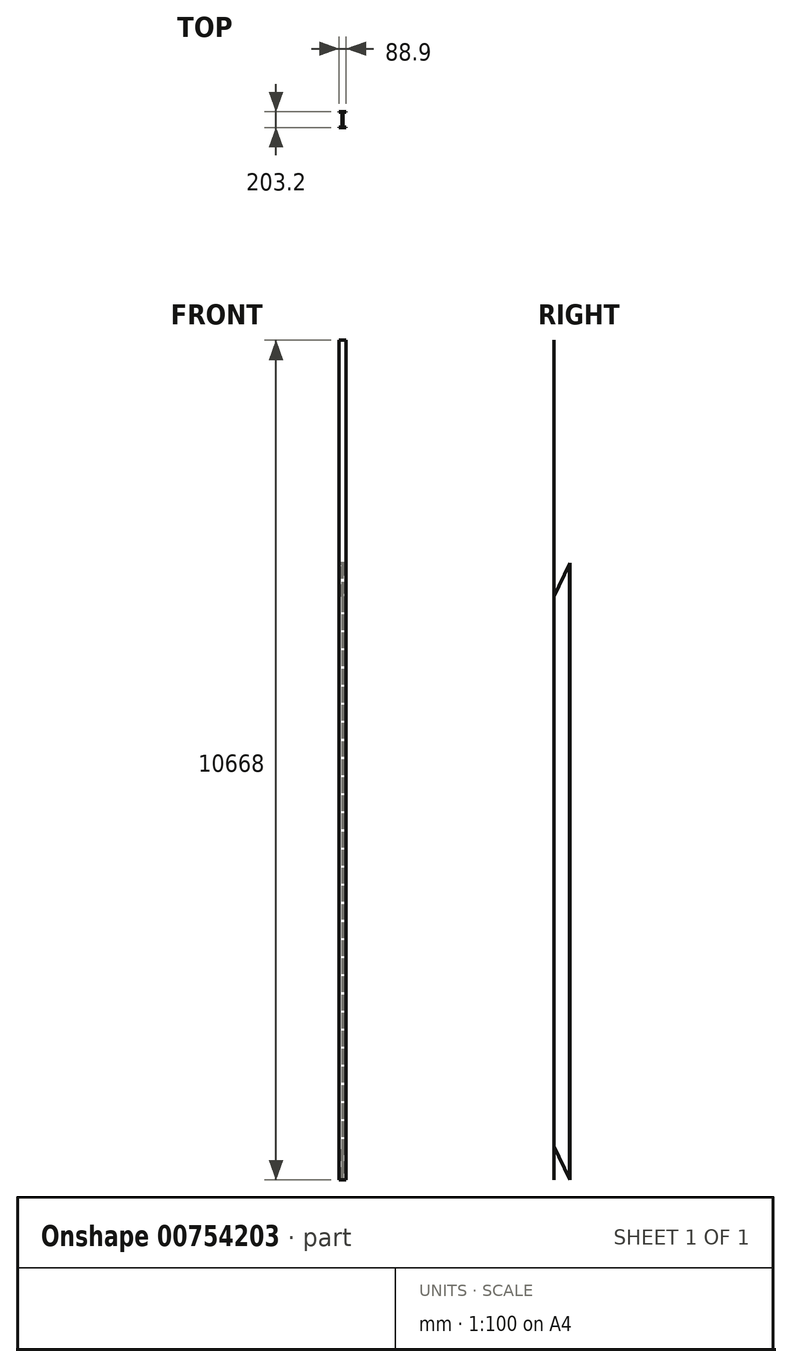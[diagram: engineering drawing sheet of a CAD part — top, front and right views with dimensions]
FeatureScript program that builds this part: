
annotation { "Feature Type Name" : "Feature", "Feature Type Description" : "" }
export const myFeature = defineFeature(function(context is Context, id is Id, definition is map)
    precondition{}
    {
        {
            var Q0;
            Q0=qCreatedBy(makeId("Top.planeOp"),FACE);
            var sketch = newSketch(context, id + "F0", { "sketchPlane" : qUnion([Q0])});
            skLineSegment(sketch, "E0.bottom", {"start": v(44.45, 101.6) * mm, "end": v(-44.45, 101.6) * mm});
            skLineSegment(sketch, "E0.top", {"start": v(44.45, -101.6) * mm, "end": v(-44.45, -101.6) * mm});
            skLineSegment(sketch, "E0.left", {"start": v(44.45, 101.6) * mm, "end": v(44.45, -101.6) * mm});
            skLineSegment(sketch, "E0.right", {"start": v(-44.45, 101.6) * mm, "end": v(-44.45, -101.6) * mm});
            skPoint(sketch, "E0.middle", {"position": v(0, 0) * mm});
            skSolve(sketch);
        }
        {
            var Q0;
            Q0=makeQuery(id+"F0.imprint","IMPRINT",FACE,{"disambiguationData":[TD([[makeQuery(id+"F0.imprint","IMPRINT",EDGE,{"derivedFrom":sQuery(id+"F0.wireOp",EDGE,"E0.bottom")}),1.0]])]});
            extrude(context, id + "F1", {"entities" : qUnion([Q0]), "depth" : 10668 * mm, "offsetDistance" : 25.4 * mm});
        }
        {
            var Q0;
            Q0=qCreatedBy(makeId("Top.planeOp"),FACE);
            var sketch = newSketch(context, id + "F2", { "sketchPlane" : qUnion([Q0])});
            skLineSegment(sketch, "E1.0.0", {"start": v(44.45, -101.6) * mm, "end": v(-44.45, -101.6) * mm, "construction": true});
            skLineSegment(sketch, "E1.0.1", {"start": v(-44.45, -101.6) * mm, "end": v(-44.45, 101.6) * mm, "construction": true});
            skLineSegment(sketch, "E1.0.2", {"start": v(-44.45, 101.6) * mm, "end": v(44.45, 101.6) * mm, "construction": true});
            skLineSegment(sketch, "E1.0.3", {"start": v(44.45, 101.6) * mm, "end": v(44.45, -101.6) * mm, "construction": true});
            skLineSegment(sketch, "E2.bottom", {"start": v(-44.45, -96.52) * mm, "end": v(-4.76, -96.52) * mm});
            skLineSegment(sketch, "E2.top", {"start": v(-44.45, 96.52) * mm, "end": v(-4.76, 96.52) * mm});
            skLineSegment(sketch, "E2.left", {"start": v(-44.45, -96.52) * mm, "end": v(-44.45, 96.52) * mm});
            skLineSegment(sketch, "E2.right", {"start": v(-4.76, -96.52) * mm, "end": v(-4.76, 96.52) * mm});
            skLineSegment(sketch, "E3.bottom", {"start": v(44.45, -96.52) * mm, "end": v(4.76, -96.52) * mm});
            skLineSegment(sketch, "E3.top", {"start": v(44.45, 96.52) * mm, "end": v(4.76, 96.52) * mm});
            skLineSegment(sketch, "E3.left", {"start": v(44.45, -96.52) * mm, "end": v(44.45, 96.52) * mm});
            skLineSegment(sketch, "E3.right", {"start": v(4.76, -96.52) * mm, "end": v(4.76, 96.52) * mm});
            skSolve(sketch);
        }
        {
            var Q0;
            Q0=makeQuery(id+"F2.imprint","IMPRINT",FACE,{"disambiguationData":[TD([[makeQuery(id+"F2.imprint","IMPRINT",EDGE,{"derivedFrom":sQuery(id+"F2.wireOp",EDGE,"E2.bottom")}),1.0]])]});
            var Q1;
            Q1=makeQuery(id+"F2.imprint","IMPRINT",FACE,{"disambiguationData":[TD([[makeQuery(id+"F2.imprint","IMPRINT",EDGE,{"derivedFrom":sQuery(id+"F2.wireOp",EDGE,"E3.bottom")}),-1.0]])]});
            extrude(context, id + "F3", {"entities" : qUnion([Q0, Q1]), "operationType" : NewBodyOperationType.REMOVE, "endBound" : BoundingType.THROUGH_ALL, "depth" : 25.4 * mm, "offsetDistance" : 25.4 * mm});
        }
        {
            var Q0;
            {var subQ1=sQuery(id+"F0.wireOp",EDGE,"E0.left");var subQ2=sQuery(id+"F0.wireOp",EDGE,"E0.top");Q0=makeQuery(id+"F3.boolean.opBoolean","SPLIT",FACE,{"disambiguationData":[TD([makeQuery(id+"F1.opExtrude","SWEPT_FACE",FACE,{"disambiguationData":[OSD([subQ2])]})])],"derivedFrom":makeQuery(id+"F1.opExtrude","SWEPT_FACE",FACE,{"disambiguationData":[OSD([subQ1])]})});}
            var sketch = newSketch(context, id + "F4", { "sketchPlane" : qUnion([Q0])});
            skLineSegment(sketch, "E4", {"start": v(-1727.2, 3918.86) * mm, "end": v(2540, -5225.14) * mm});
            skLineSegment(sketch, "E5", {"start": v(2540, -5225.14) * mm, "end": v(7416.8, -5225.14) * mm, "construction": true});
            skLineSegment(sketch, "E6", {"start": v(7416.8, -5225.14) * mm, "end": v(7416.8, 13062.86) * mm, "construction": true});
            skLineSegment(sketch, "E7", {"start": v(7416.8, 13062.86) * mm, "end": v(2540, 13062.86) * mm, "construction": true});
            skLineSegment(sketch, "E8", {"start": v(2540, 13062.86) * mm, "end": v(-1727.2, 3918.86) * mm});
            skPoint(sketch, "E9.0", {"position": v(101.6, 0) * mm});
            skLineSegment(sketch, "E10", {"start": v(2540, 13062.86) * mm, "end": v(-1612.56, 13062.86) * mm});
            skLineSegment(sketch, "E11", {"start": v(-1612.56, 13062.86) * mm, "end": v(-1727.2, 3918.86) * mm});
            skLineSegment(sketch, "E12", {"start": v(-1727.2, -5225.14) * mm, "end": v(2540, -5225.14) * mm});
            skLineSegment(sketch, "E13", {"start": v(-1727.2, 3918.86) * mm, "end": v(-1727.2, -5225.14) * mm});
            skSolve(sketch);
        }
        {
            var Q0;
            {var subQ1=sQuery(id+"F4.wireOp",EDGE,"E10");Q0=makeQuery(id+"F4.imprint","IMPRINT",FACE,{"disambiguationData":[TD([[makeQuery(id+"F4.imprint","IMPRINT",EDGE,{"derivedFrom":subQ1}),1.0]])]});}
            var Q1;
            {var subQ0=sQuery(id+"F4.wireOp",EDGE,"E8");var subQ1=sQuery(id+"F2.wireOp",EDGE,"E3.bottom");var subQ2=makeQuery(id+"F3.boolean.opBoolean","COPY",EDGE,{"derivedFrom":makeQuery(id+"F3.opExtrude","SWEPT_EDGE",EDGE,{"disambiguationData":[OSD([subQ1,sQuery(id+"F2.wireOp",EDGE,"E3.left")])]})});var subQ3=makeQuery(id+"F4.imprint","INTERSECT",VERTEX,{"derivedFrom":[subQ2,subQ0]});Q1=makeQuery(id+"F4.imprint","IMPRINT",FACE,{"disambiguationData":[TD([[makeQuery(id+"F4.imprint","IMPRINT",EDGE,{"disambiguationData":[TD([[subQ3,-1.0]])],"derivedFrom":subQ0}),-1.0]])]});}
            var Q2;
            {var subQ1=sQuery(id+"F4.wireOp",EDGE,"E12");Q2=makeQuery(id+"F4.imprint","IMPRINT",FACE,{"disambiguationData":[TD([[makeQuery(id+"F4.imprint","IMPRINT",EDGE,{"derivedFrom":subQ1}),1.0]])]});}
            var Q3;
            {var subQ0=sQuery(id+"F4.wireOp",EDGE,"E4");var subQ1=sQuery(id+"F2.wireOp",EDGE,"E3.bottom");var subQ2=makeQuery(id+"F3.boolean.opBoolean","COPY",EDGE,{"derivedFrom":makeQuery(id+"F3.opExtrude","SWEPT_EDGE",EDGE,{"disambiguationData":[OSD([subQ1,sQuery(id+"F2.wireOp",EDGE,"E3.left")])]})});var subQ3=makeQuery(id+"F4.imprint","INTERSECT",VERTEX,{"derivedFrom":[subQ2,subQ0]});Q3=makeQuery(id+"F4.imprint","IMPRINT",FACE,{"disambiguationData":[TD([[makeQuery(id+"F4.imprint","IMPRINT",EDGE,{"disambiguationData":[TD([[subQ3,1.0]])],"derivedFrom":subQ0}),-1.0]])]});}
            extrude(context, id + "F5", {"entities" : qUnion([Q0, Q1, Q2, Q3]), "operationType" : NewBodyOperationType.REMOVE, "endBound" : BoundingType.THROUGH_ALL, "oppositeDirection" : true, "depth" : 25.4 * mm, "offsetDistance" : 25.4 * mm});
        }
    });
